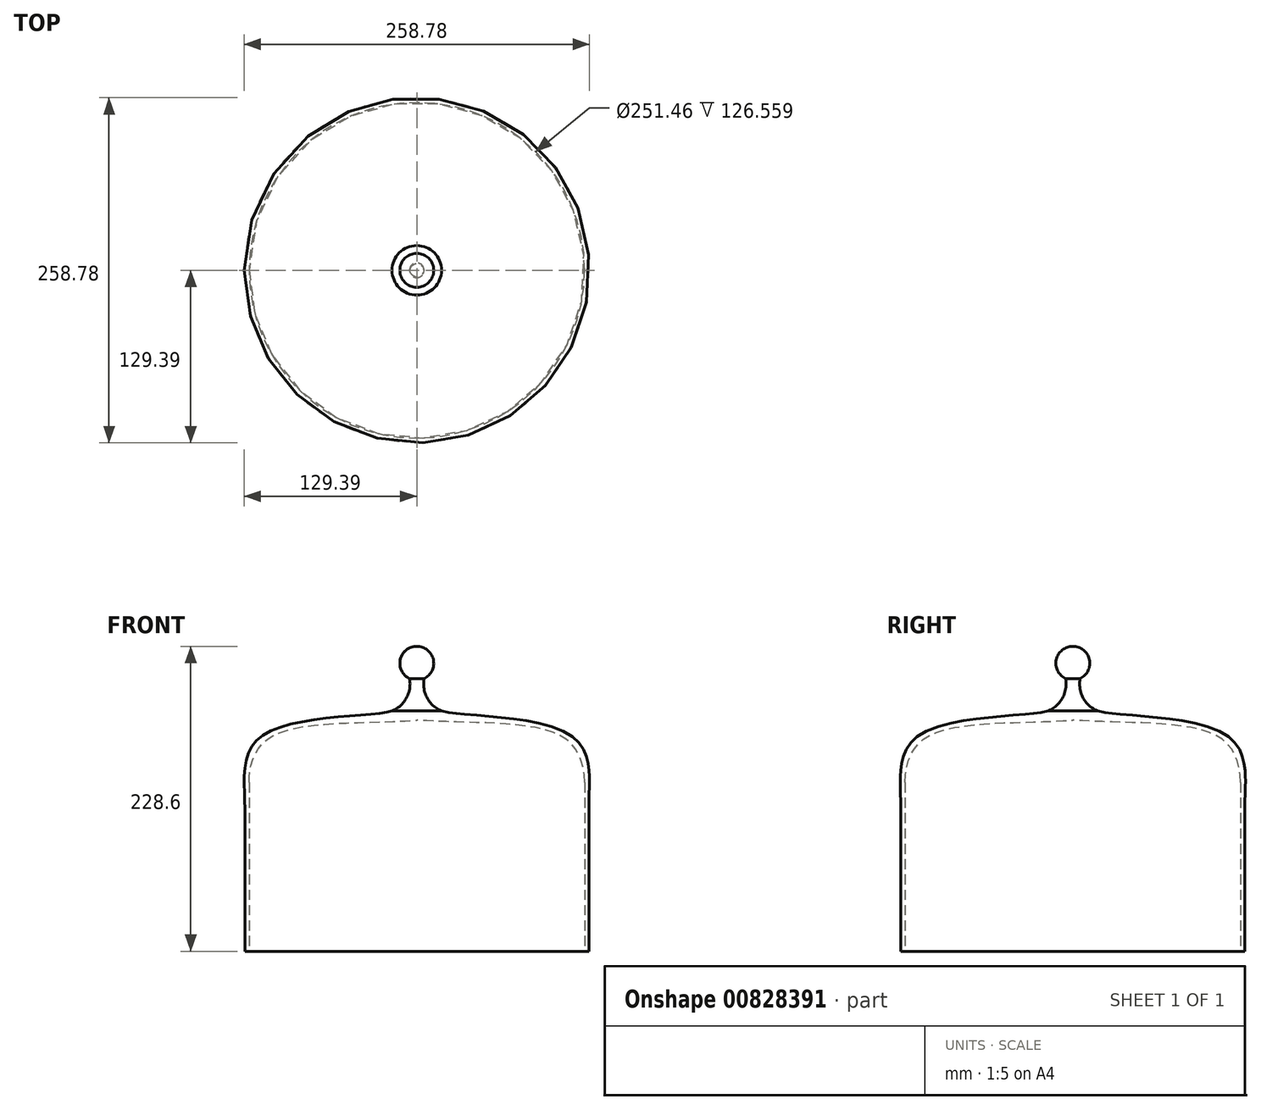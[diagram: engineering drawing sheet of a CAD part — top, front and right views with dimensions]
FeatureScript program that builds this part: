
annotation { "Feature Type Name" : "Feature", "Feature Type Description" : "" }
export const myFeature = defineFeature(function(context is Context, id is Id, definition is map)
    precondition{}
    {
        {
            var Q0;
            Q0=qCreatedBy(makeId("Front.planeOp"),FACE);
            var sketch = newSketch(context, id + "F0", { "sketchPlane" : qUnion([Q0])});
            skLineSegment(sketch, "E0", {"start": v(-128.9, 0) * mm, "end": v(-128.9, 106.9) * mm});
            skFitSpline(sketch, "E1", {"points": [v(-128.9, 106.9) * mm, v(-116.14, 161.36) * mm, v(-18.55, 180.2) * mm], "startDerivative": vector(0, 136.62) * mm, "endDerivative": vector(74.35, 24.42) * mm});
            skArc(sketch, "E2", {"start": v(0, 228.6) * mm, "mid": v(-12.39, 218.71) * mm, "end": v(-5.48, 204.44) * mm});
            skArc(sketch, "E3", {"start": v(-18.55, 180.2) * mm, "mid": v(-7.7, 190) * mm, "end": v(-5.48, 204.44) * mm});
            skLineSegment(sketch, "E4", {"start": v(0, 0) * mm, "end": v(0, 228.6) * mm, "construction": true});
            skLineSegment(sketch, "E5", {"start": v(-125.73, 0) * mm, "end": v(-125.73, 126.56) * mm});
            skFitSpline(sketch, "E6", {"points": [v(-125.73, 126.56) * mm, v(-111.04, 159.53) * mm, v(0, 173.27) * mm], "startDerivative": vector(0, 91.1) * mm, "endDerivative": vector(203.37, 14.77) * mm});
            skLineSegment(sketch, "E7", {"start": v(-128.9, 0) * mm, "end": v(-125.73, 0) * mm});
            skLineSegment(sketch, "E8", {"start": v(0, 228.6) * mm, "end": v(0, 173.27) * mm});
            skSolve(sketch);
        }
        {
            var Q0;
            Q0 = qSketchRegion(id + "F0", true);
            var Q1;
            Q1=sQuery(id+"F0.wireOp",EDGE,"E4");
            revolve(context, id + "F1", {"surfaceOperationType" : NewSurfaceOperationType.NEW, "entities" : qUnion([Q0]), "axis" : qUnion([Q1]), "revolveType" : RevolveType.FULL});
        }
    });
